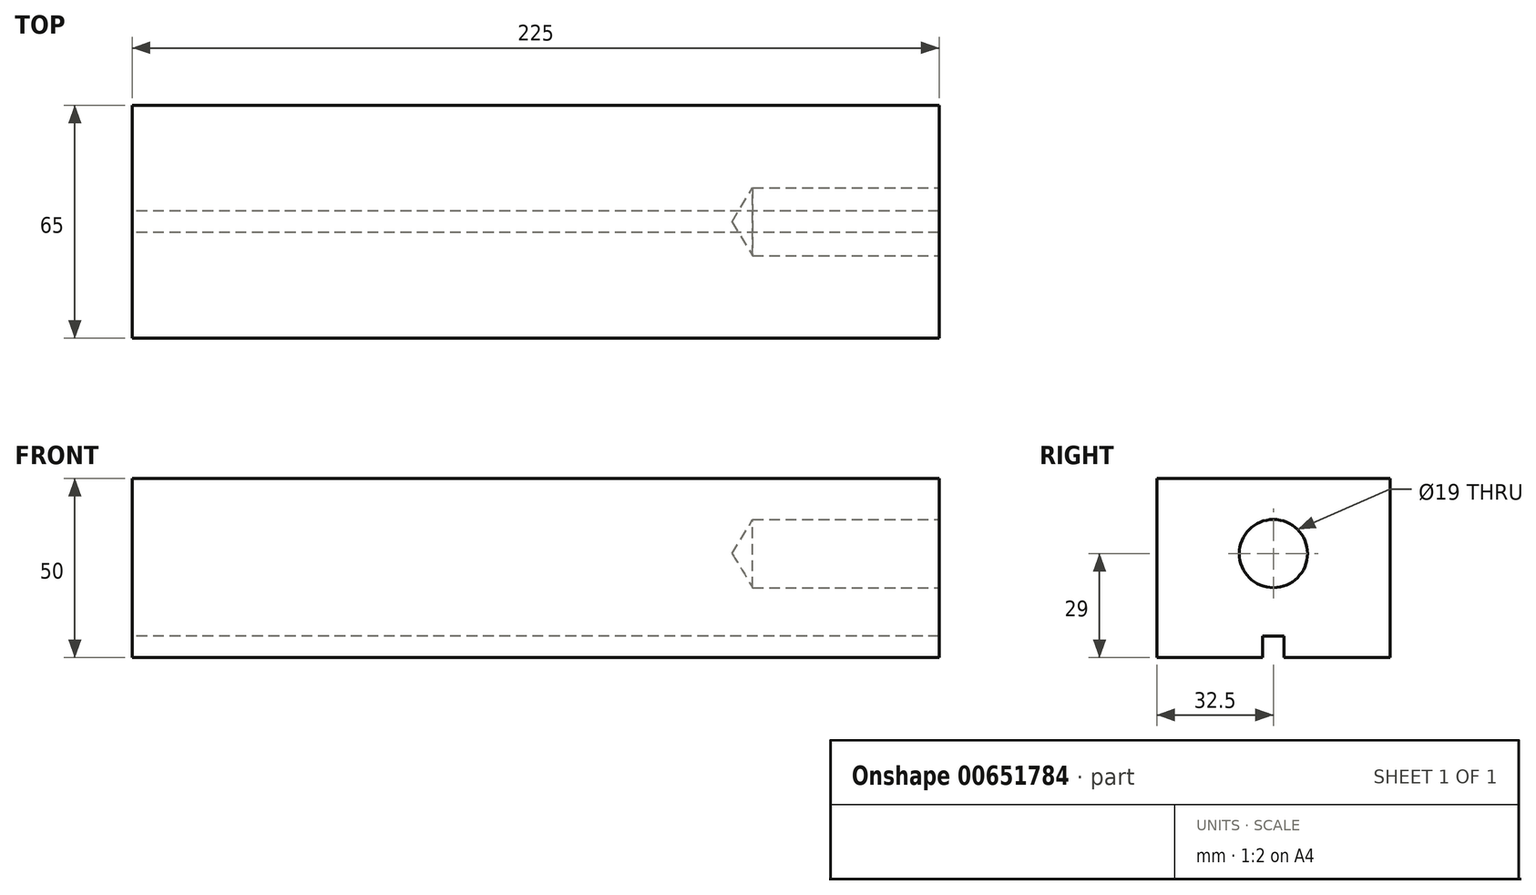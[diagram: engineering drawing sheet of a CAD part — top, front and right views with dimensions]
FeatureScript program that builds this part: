
annotation { "Feature Type Name" : "Feature", "Feature Type Description" : "" }
export const myFeature = defineFeature(function(context is Context, id is Id, definition is map)
    precondition{}
    {
        {
            var Q0;
            Q0=qCreatedBy(makeId("Right.planeOp"),FACE);
            var sketch = newSketch(context, id + "F0", { "sketchPlane" : qUnion([Q0])});
            skLineSegment(sketch, "E0.bottom", {"start": v(3, -29) * mm, "end": v(32.5, -29) * mm});
            skLineSegment(sketch, "E0.top", {"start": v(0, 21) * mm, "end": v(32.5, 21) * mm});
            skLineSegment(sketch, "E0.left", {"start": v(0, -23) * mm, "end": v(0, 21) * mm});
            skLineSegment(sketch, "E0.right", {"start": v(32.5, -29) * mm, "end": v(32.5, 21) * mm});
            skLineSegment(sketch, "E1.top", {"start": v(0, -23) * mm, "end": v(3, -23) * mm});
            skLineSegment(sketch, "E1.right", {"start": v(3, -29) * mm, "end": v(3, -23) * mm});
            skSolve(sketch);
        }
        {
            var Q0;
            Q0=makeQuery(id+"F0.imprint","IMPRINT",FACE,{"disambiguationData":[TD([[makeQuery(id+"F0.imprint","IMPRINT",EDGE,{"derivedFrom":sQuery(id+"F0.wireOp",EDGE,"E0.bottom")}),1.0]])]});
            extrude(context, id + "F1", {"entities" : qUnion([Q0]), "endBound" : BoundingType.SYMMETRIC, "depth" : 225 * mm, "offsetDistance" : 25 * mm});
        }
        {
            var Q0;
            Q0=makeQuery(id+"F1.opExtrude","CAP_FACE",FACE,{"disambiguationData":[OSD([sQuery(id+"F0.wireOp",EDGE,"E0.bottom"),sQuery(id+"F0.wireOp",EDGE,"E0.top"),sQuery(id+"F0.wireOp",EDGE,"E0.left"),sQuery(id+"F0.wireOp",EDGE,"E0.right"),sQuery(id+"F0.wireOp",EDGE,"E1.top"),sQuery(id+"F0.wireOp",EDGE,"E1.right")])],"isStart":false});
            var sketch = newSketch(context, id + "F2", { "sketchPlane" : qUnion([Q0])});
            skLineSegment(sketch, "E2", {"start": v(32.5, -29) * mm, "end": v(32.5, 0) * mm, "construction": true});
            skLineSegment(sketch, "E3", {"start": v(32.5, 0) * mm, "end": v(0, 0) * mm, "construction": true});
            skPoint(sketch, "E4", {"position": v(0, 0) * mm});
            skSolve(sketch);
        }
        {
            var Q0;
            Q0=sQuery(id+"F2.wireOp",VERTEX,"E4");
            var Q1;
            Q1=makeQuery(id+"F1.opExtrude","SWEPT_BODY",BODY,{"disambiguationData":[OSD([sQuery(id+"F0.wireOp",EDGE,"E0.bottom"),sQuery(id+"F0.wireOp",EDGE,"E0.top"),sQuery(id+"F0.wireOp",EDGE,"E0.left"),sQuery(id+"F0.wireOp",EDGE,"E0.right"),sQuery(id+"F0.wireOp",EDGE,"E1.top"),sQuery(id+"F0.wireOp",EDGE,"E1.right")])]});
            hole(context, id + "F3", {"style" : HoleStyle.SIMPLE, "endStyle" : HoleEndStyle.BLIND, "holeDiameter" : 19 * mm, "majorDiameter" : 5 * mm, "holeDepth" : 52 * mm, "isTappedThrough" : true, "tappedDepth" : 12 * mm, "tapClearance" : 3, "startFromSketch" : true, "locations" : qUnion([Q0]), "scope" : qUnion([Q1])});
        }
        {
            var Q0;
            Q0=makeQuery(id+"F1.opExtrude","SWEPT_BODY",BODY,{"disambiguationData":[OSD([sQuery(id+"F0.wireOp",EDGE,"E0.bottom"),sQuery(id+"F0.wireOp",EDGE,"E0.top"),sQuery(id+"F0.wireOp",EDGE,"E0.left"),sQuery(id+"F0.wireOp",EDGE,"E0.right"),sQuery(id+"F0.wireOp",EDGE,"E1.top"),sQuery(id+"F0.wireOp",EDGE,"E1.right")])]});
            var Q1;
            Q1=makeQuery(id+"F1.opExtrude","SWEPT_FACE",FACE,{"disambiguationData":[OSD([sQuery(id+"F0.wireOp",EDGE,"E0.left")])]});
            mirror(context, id + "F4", {"operationType" : NewBodyOperationType.ADD, "entities" : qUnion([Q0]), "mirrorPlane" : qUnion([Q1])});
        }
    });
